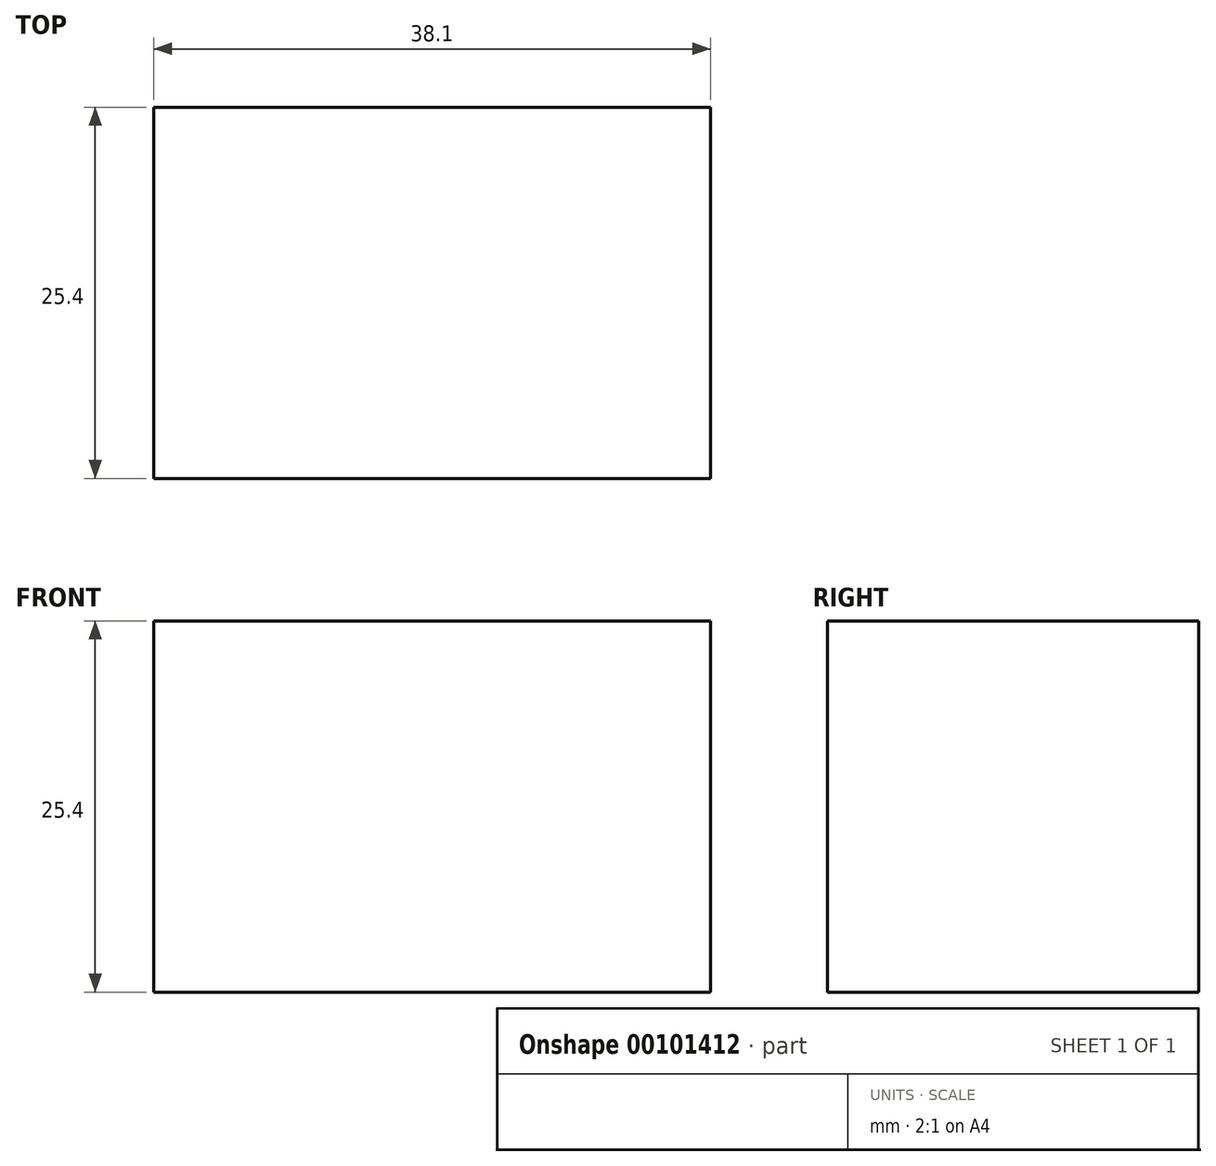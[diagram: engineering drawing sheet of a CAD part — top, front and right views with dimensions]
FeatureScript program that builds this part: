
annotation { "Feature Type Name" : "Feature", "Feature Type Description" : "" }
export const myFeature = defineFeature(function(context is Context, id is Id, definition is map)
    precondition{}
    {
        {
            var Q0;
            Q0=qCreatedBy(makeId("Front.planeOp"),FACE);
            var sketch = newSketch(context, id + "F0", { "sketchPlane" : qUnion([Q0])});
            skLineSegment(sketch, "E0", {"start": v(0, 0) * mm, "end": v(25.4, 0) * mm});
            skLineSegment(sketch, "E1", {"start": v(25.4, 0) * mm, "end": v(25.4, 12.7) * mm});
            skLineSegment(sketch, "E2", {"start": v(25.4, 12.7) * mm, "end": v(38.1, 12.7) * mm});
            skLineSegment(sketch, "E3", {"start": v(38.1, 12.7) * mm, "end": v(38.1, 0) * mm});
            skLineSegment(sketch, "E4", {"start": v(38.1, 0) * mm, "end": v(25.4, 0) * mm});
            skLineSegment(sketch, "E5", {"start": v(38.1, 12.7) * mm, "end": v(38.1, 25.4) * mm});
            skLineSegment(sketch, "E6", {"start": v(38.1, 25.4) * mm, "end": v(12.7, 25.4) * mm});
            skLineSegment(sketch, "E7", {"start": v(12.7, 25.4) * mm, "end": v(12.7, 0) * mm});
            skLineSegment(sketch, "E8", {"start": v(0, 0) * mm, "end": v(0, 25.4) * mm});
            skLineSegment(sketch, "E9", {"start": v(0, 25.4) * mm, "end": v(12.7, 25.4) * mm});
            skSolve(sketch);
        }
        {
            var Q0;
            Q0 = qSketchRegion(id + "F0", true);
            extrude(context, id + "F1", {"entities" : qUnion([Q0]), "oppositeDirection" : true, "depth" : 25.4 * mm});
        }
    });
